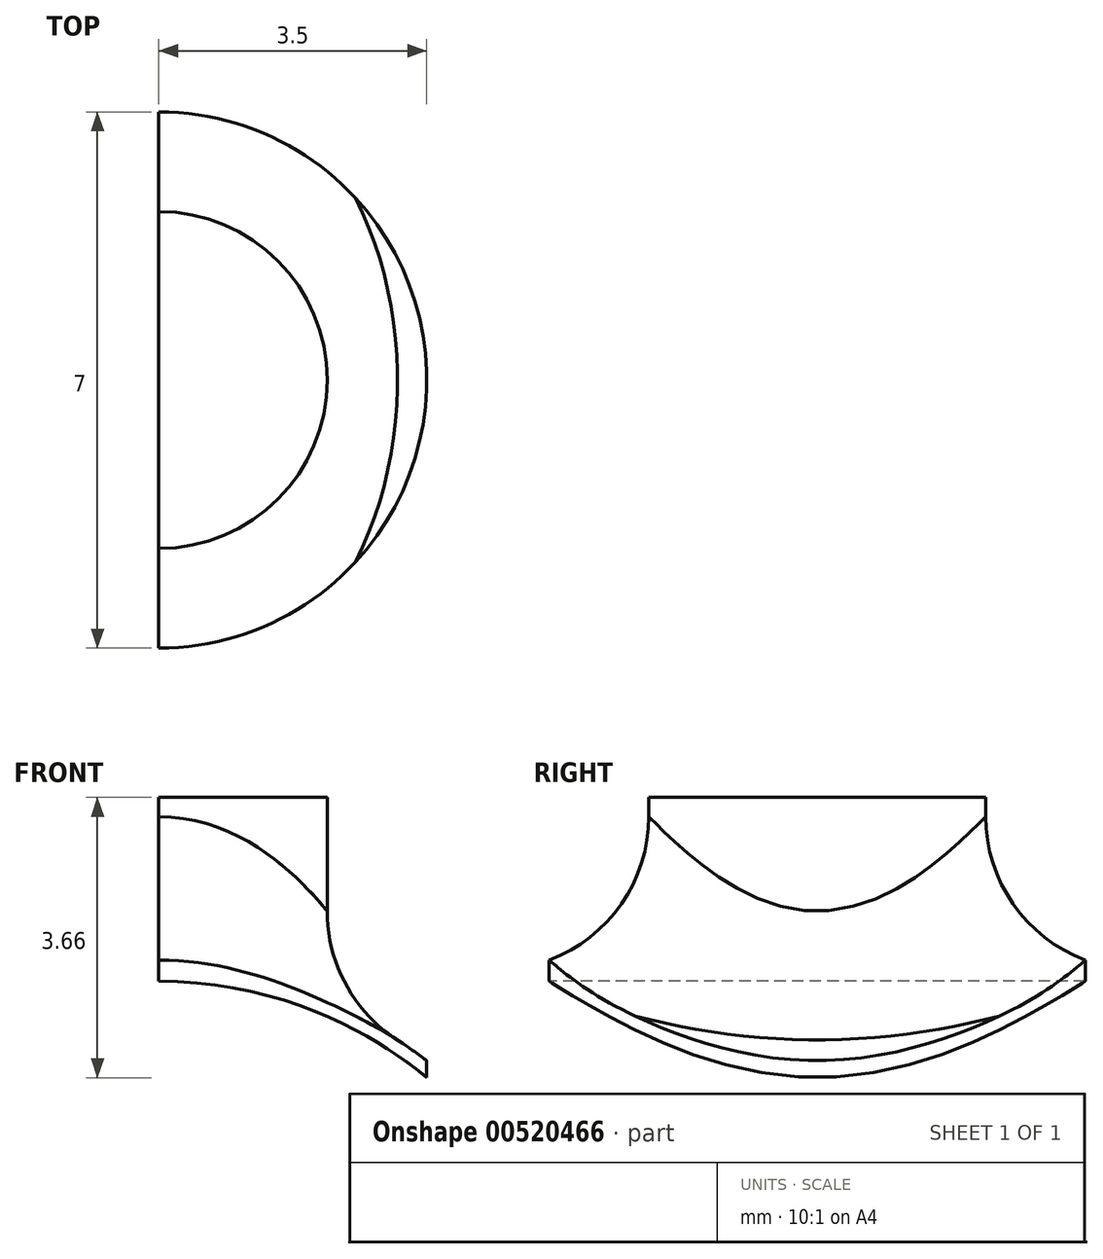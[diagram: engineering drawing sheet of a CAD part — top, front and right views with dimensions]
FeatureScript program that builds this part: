
annotation { "Feature Type Name" : "Feature", "Feature Type Description" : "" }
export const myFeature = defineFeature(function(context is Context, id is Id, definition is map)
    precondition{}
    {
        {
            var Q0;
            Q0=qCreatedBy(makeId("Top.planeOp"),FACE);
            var sketch = newSketch(context, id + "F0", { "sketchPlane" : qUnion([Q0])});
            skArc(sketch, "E0", {"start": v(2.2, 0) * mm, "mid": v(1.56, 1.56) * mm, "end": v(0, 2.2) * mm});
            skLineSegment(sketch, "E1", {"start": v(0, 0) * mm, "end": v(0, 2.2) * mm});
            skLineSegment(sketch, "E2", {"start": v(0, 0) * mm, "end": v(2.2, 0) * mm});
            skSolve(sketch);
        }
        {
            var Q0;
            Q0=makeQuery(id+"F0.imprint","IMPRINT",FACE,{"disambiguationData":[TD([[makeQuery(id+"F0.imprint","IMPRINT",EDGE,{"derivedFrom":sQuery(id+"F0.wireOp",EDGE,"E0")}),1.0]])]});
            extrude(context, id + "F1", {"entities" : qUnion([Q0]), "depth" : 8 * mm, "offsetDistance" : 25.4 * mm});
        }
        {
            var Q0;
            Q0=makeQuery(id+"F1.opExtrude","SWEPT_FACE",FACE,{"disambiguationData":[OSD([sQuery(id+"F0.wireOp",EDGE,"E2")])]});
            var sketch = newSketch(context, id + "F2", { "sketchPlane" : qUnion([Q0])});
            skCircle(sketch, "E3", {"center": v(0, 0) * mm, "radius": 5.75 * mm});
            skLineSegment(sketch, "E4", {"start": v(0, 0) * mm, "end": v(0, 5.75) * mm});
            skLineSegment(sketch, "E5", {"start": v(0, 0) * mm, "end": v(5.75, 0) * mm});
            skSolve(sketch);
        }
        {
            var Q0;
            {var subQ0=sQuery(id+"F2.wireOp",EDGE,"E5");var subQ1=sQuery(id+"F2.wireOp",EDGE,"E3");var subQ2=makeQuery(id+"F2.imprint","INTERSECT",VERTEX,{"derivedFrom":[subQ1,subQ0]});Q0=makeQuery(id+"F2.imprint","IMPRINT",FACE,{"disambiguationData":[TD([[makeQuery(id+"F2.imprint","IMPRINT",EDGE,{"disambiguationData":[TD([[subQ2,-1.0]])],"derivedFrom":subQ1}),1.0]])]});}
            var Q1;
            {var subQ0=sQuery(id+"F2.wireOp",EDGE,"E4");Q1=makeQuery(id+"F2.imprint","IMPRINT",FACE,{"disambiguationData":[TD([[makeQuery(id+"F2.imprint","IMPRINT",EDGE,{"derivedFrom":subQ0}),1.0]])]});}
            var Q2;
            Q2=sQuery(id+"F2.wireOp",EDGE,"E5");
            extrude(context, id + "F3", {"entities" : qUnion([Q0, Q1]), "operationType" : NewBodyOperationType.ADD, "surfaceEntities" : qUnion([Q2]), "oppositeDirection" : true, "depth" : 6 * mm, "offsetDistance" : 25 * mm});
        }
        {
            var Q0;
            Q0=makeQuery(id+"F3.boolean.opBoolean","MERGE",FACE,{"derivedFrom":[makeQuery(id+"F1.opExtrude","CAP_FACE",FACE,{"disambiguationData":[OSD([sQuery(id+"F0.wireOp",EDGE,"E0"),sQuery(id+"F0.wireOp",EDGE,"E1"),sQuery(id+"F0.wireOp",EDGE,"E2")])],"isStart":true}),makeQuery(id+"F3.opExtrude","SWEPT_FACE",FACE,{"disambiguationData":[OSD([sQuery(id+"F2.wireOp",EDGE,"E5")])]})]});
            var sketch = newSketch(context, id + "F4", { "sketchPlane" : qUnion([Q0])});
            skCircle(sketch, "E6", {"center": v(0, 0) * mm, "radius": 3.5 * mm});
            skCircle(sketch, "E7", {"center": v(0, 0) * mm, "radius": 15.02 * mm});
            skSolve(sketch);
        }
        {
            var Q0;
            Q0=makeQuery(id+"F4.imprint","IMPRINT",FACE,{"disambiguationData":[TD([[makeQuery(id+"F4.imprint","IMPRINT",EDGE,{"derivedFrom":sQuery(id+"F4.wireOp",EDGE,"E7")}),1.0]])]});
            var Q1;
            {var subQ0=sQuery(id+"F2.wireOp",EDGE,"E5");var subQ1=makeQuery(id+"F3.opExtrude","CAP_EDGE",EDGE,{"disambiguationData":[OSD([subQ0])],"isStart":false});Q1=makeQuery(id+"F4.imprint","IMPRINT",FACE,{"disambiguationData":[TD([[makeQuery(id+"F4.imprint","IMPRINT",EDGE,{"derivedFrom":subQ1}),1.0]])]});}
            extrude(context, id + "F5", {"entities" : qUnion([Q0, Q1]), "operationType" : NewBodyOperationType.REMOVE, "oppositeDirection" : true, "depth" : 25 * mm, "offsetDistance" : 25 * mm});
        }
        {
            var Q0;
            Q0=makeQuery(id+"F3.boolean.opBoolean","INTERSECT",EDGE,{"derivedFrom":[makeQuery(id+"F1.opExtrude","SWEPT_FACE",FACE,{"disambiguationData":[OSD([sQuery(id+"F0.wireOp",EDGE,"E0")])]}),makeQuery(id+"F3.opExtrude","SWEPT_FACE",FACE,{"disambiguationData":[OSD([sQuery(id+"F2.wireOp",EDGE,"E3")])]})]});
            fillet(context, id + "F6", {"entities" : qUnion([Q0]), "radius" : 2 * mm, "tangentPropagation" : true, "allowEdgeOverflow" : false});
        }
        {
            var Q0;
            Q0=makeQuery(id+"F3.boolean.opBoolean","MERGE",FACE,{"derivedFrom":[makeQuery(id+"F1.opExtrude","SWEPT_FACE",FACE,{"disambiguationData":[OSD([sQuery(id+"F0.wireOp",EDGE,"E2")])]}),makeQuery(id+"F3.opExtrude","CAP_FACE",FACE,{"disambiguationData":[OSD([sQuery(id+"F2.wireOp",EDGE,"E3"),sQuery(id+"F2.wireOp",EDGE,"E4"),sQuery(id+"F2.wireOp",EDGE,"E5")])],"isStart":true})]});
            var sketch = newSketch(context, id + "F7", { "sketchPlane" : qUnion([Q0])});
            skCircle(sketch, "E8", {"center": v(0, 0.1) * mm, "radius": 5.5 * mm});
            skSolve(sketch);
        }
        {
            var Q0;
            {var subQ1=sQuery(id+"F0.wireOp",EDGE,"E2");var subQ4=sQuery(id+"F2.wireOp",EDGE,"E5");var subQ7=makeQuery(id+"F3.boolean.opBoolean","MERGE",EDGE,{"derivedFrom":[makeQuery(id+"F1.opExtrude","CAP_EDGE",EDGE,{"disambiguationData":[OSD([subQ1])],"isStart":true}),makeQuery(id+"F3.opExtrude","CAP_EDGE",EDGE,{"disambiguationData":[OSD([subQ4])],"isStart":true})]});Q0=makeQuery(id+"F7.imprint","IMPRINT",FACE,{"disambiguationData":[TD([[makeQuery(id+"F7.imprint","IMPRINT",EDGE,{"derivedFrom":subQ7}),-1.0]])]});}
            var Q1;
            {var subQ1=sQuery(id+"F0.wireOp",EDGE,"E2");var subQ4=sQuery(id+"F2.wireOp",EDGE,"E5");var subQ7=makeQuery(id+"F3.boolean.opBoolean","MERGE",EDGE,{"derivedFrom":[makeQuery(id+"F1.opExtrude","CAP_EDGE",EDGE,{"disambiguationData":[OSD([subQ1])],"isStart":true}),makeQuery(id+"F3.opExtrude","CAP_EDGE",EDGE,{"disambiguationData":[OSD([subQ4])],"isStart":true})]});Q1=makeQuery(id+"F7.imprint","IMPRINT",FACE,{"disambiguationData":[TD([[makeQuery(id+"F7.imprint","IMPRINT",EDGE,{"derivedFrom":subQ7}),1.0]])]});}
            extrude(context, id + "F8", {"entities" : qUnion([Q0, Q1]), "operationType" : NewBodyOperationType.REMOVE, "oppositeDirection" : true, "depth" : 25 * mm, "offsetDistance" : 25 * mm});
        }
        {
            var Q0;
            Q0=makeQuery(id+"F1.opExtrude","SWEPT_BODY",BODY,{"disambiguationData":[OSD([sQuery(id+"F0.wireOp",EDGE,"E0"),sQuery(id+"F0.wireOp",EDGE,"E1"),sQuery(id+"F0.wireOp",EDGE,"E2")])]});
            var Q1;
            Q1=makeQuery(id+"F3.boolean.opBoolean","MERGE",FACE,{"derivedFrom":[makeQuery(id+"F1.opExtrude","SWEPT_FACE",FACE,{"disambiguationData":[OSD([sQuery(id+"F0.wireOp",EDGE,"E2")])]}),makeQuery(id+"F3.opExtrude","CAP_FACE",FACE,{"disambiguationData":[OSD([sQuery(id+"F2.wireOp",EDGE,"E3"),sQuery(id+"F2.wireOp",EDGE,"E4"),sQuery(id+"F2.wireOp",EDGE,"E5")])],"isStart":true})]});
            mirror(context, id + "F9", {"operationType" : NewBodyOperationType.ADD, "entities" : qUnion([Q0]), "mirrorPlane" : qUnion([Q1])});
        }
    });
